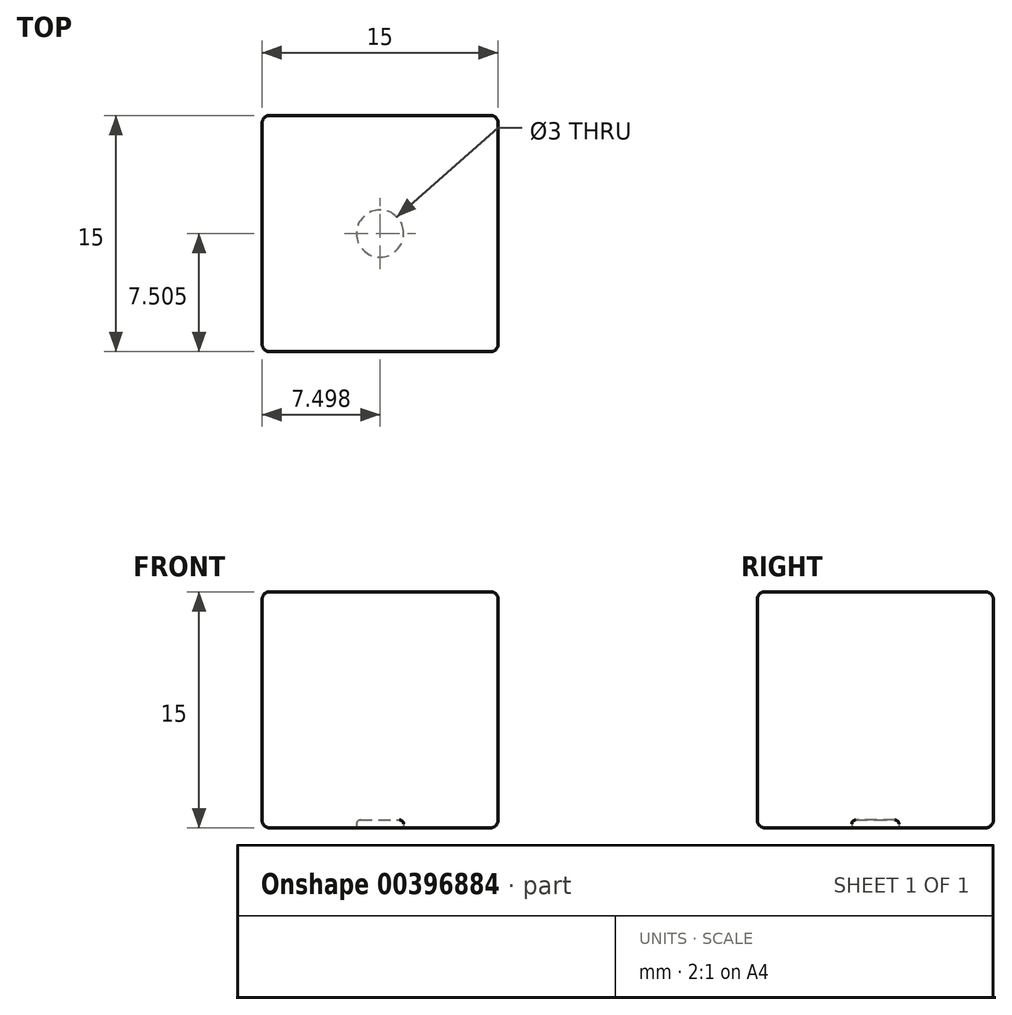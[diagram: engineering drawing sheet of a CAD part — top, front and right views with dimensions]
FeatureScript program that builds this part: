
annotation { "Feature Type Name" : "Feature", "Feature Type Description" : "" }
export const myFeature = defineFeature(function(context is Context, id is Id, definition is map)
    precondition{}
    {
        {
            var Q0;
            Q0=qCreatedBy(makeId("Top.planeOp"),FACE);
            var sketch = newSketch(context, id + "F0", { "sketchPlane" : qUnion([Q0])});
            skLineSegment(sketch, "E0.bottom", {"start": v(-9.53, -9.56) * mm, "end": v(5.47, -9.56) * mm});
            skLineSegment(sketch, "E0.top", {"start": v(-9.53, 5.44) * mm, "end": v(5.47, 5.44) * mm});
            skLineSegment(sketch, "E0.left", {"start": v(-9.53, -9.56) * mm, "end": v(-9.53, 5.44) * mm});
            skLineSegment(sketch, "E0.right", {"start": v(5.47, -9.56) * mm, "end": v(5.47, 5.44) * mm});
            skSolve(sketch);
        }
        {
            var Q0;
            Q0=makeQuery(id+"F0.imprint","IMPRINT",FACE,{"disambiguationData":[TD([[makeQuery(id+"F0.imprint","IMPRINT",EDGE,{"derivedFrom":sQuery(id+"F0.wireOp",EDGE,"E0.bottom")}),1.0]])]});
            var Q1;
            Q1=makeQuery(id+"F0.imprint","IMPRINT",FACE,{"disambiguationData":[TD([[makeQuery(id+"F0.imprint","IMPRINT",EDGE,{"derivedFrom":sQuery(id+"F0.wireOp",EDGE,"6saIbGSl-1DAX-xkG8-rUnz-SKyQh94YWWxh")}),1.0]])]});
            extrude(context, id + "F1", {"entities" : qUnion([Q0, Q1]), "depth" : 15 * mm});
        }
        {
            var Q0;
            Q0=makeQuery(id+"F1.opExtrude","CAP_FACE",FACE,{"disambiguationData":[OSD([sQuery(id+"F0.wireOp",EDGE,"E0.bottom"),sQuery(id+"F0.wireOp",EDGE,"E0.top"),sQuery(id+"F0.wireOp",EDGE,"E0.left"),sQuery(id+"F0.wireOp",EDGE,"E0.right")])],"isStart":true});
            var sketch = newSketch(context, id + "F2", { "sketchPlane" : qUnion([Q0])});
            skCircle(sketch, "E1", {"center": v(-2.03, 2.06) * mm, "radius": 1.5 * mm});
            skSolve(sketch);
        }
        {
            var Q0;
            Q0 = qSketchRegion(id + "F2", true);
            extrude(context, id + "F3", {"entities" : qUnion([Q0]), "operationType" : NewBodyOperationType.REMOVE, "oppositeDirection" : true, "depth" : 0.5 * mm});
        }
        {
            var Q0;
            Q0=makeQuery(id+"F1.opExtrude","SWEPT_EDGE",EDGE,{"disambiguationData":[OSD([sQuery(id+"F0.wireOp",EDGE,"E0.top"),sQuery(id+"F0.wireOp",EDGE,"E0.right")])]});
            var Q1;
            Q1=makeQuery(id+"F1.opExtrude","CAP_EDGE",EDGE,{"disambiguationData":[OSD([sQuery(id+"F0.wireOp",EDGE,"E0.top")])],"isStart":true});
            var Q2;
            Q2=makeQuery(id+"F1.opExtrude","CAP_EDGE",EDGE,{"disambiguationData":[OSD([sQuery(id+"F0.wireOp",EDGE,"E0.top")])],"isStart":false});
            var Q3;
            Q3=makeQuery(id+"F1.opExtrude","SWEPT_EDGE",EDGE,{"disambiguationData":[OSD([sQuery(id+"F0.wireOp",EDGE,"E0.top"),sQuery(id+"F0.wireOp",EDGE,"E0.left")])]});
            var Q4;
            Q4=makeQuery(id+"F1.opExtrude","CAP_EDGE",EDGE,{"disambiguationData":[OSD([sQuery(id+"F0.wireOp",EDGE,"E0.right")])],"isStart":true});
            var Q5;
            Q5=makeQuery(id+"F1.opExtrude","CAP_EDGE",EDGE,{"disambiguationData":[OSD([sQuery(id+"F0.wireOp",EDGE,"E0.right")])],"isStart":false});
            var Q6;
            Q6=makeQuery(id+"F1.opExtrude","SWEPT_EDGE",EDGE,{"disambiguationData":[OSD([sQuery(id+"F0.wireOp",EDGE,"E0.bottom"),sQuery(id+"F0.wireOp",EDGE,"E0.right")])]});
            var Q7;
            Q7=makeQuery(id+"F1.opExtrude","CAP_EDGE",EDGE,{"disambiguationData":[OSD([sQuery(id+"F0.wireOp",EDGE,"E0.left")])],"isStart":true});
            var Q8;
            Q8=makeQuery(id+"F1.opExtrude","CAP_EDGE",EDGE,{"disambiguationData":[OSD([sQuery(id+"F0.wireOp",EDGE,"E0.bottom")])],"isStart":true});
            var Q9;
            Q9=makeQuery(id+"F1.opExtrude","CAP_EDGE",EDGE,{"disambiguationData":[OSD([sQuery(id+"F0.wireOp",EDGE,"E0.left")])],"isStart":false});
            var Q10;
            Q10=makeQuery(id+"F1.opExtrude","SWEPT_EDGE",EDGE,{"disambiguationData":[OSD([sQuery(id+"F0.wireOp",EDGE,"E0.bottom"),sQuery(id+"F0.wireOp",EDGE,"E0.left")])]});
            var Q11;
            Q11=makeQuery(id+"F1.opExtrude","CAP_EDGE",EDGE,{"disambiguationData":[OSD([sQuery(id+"F0.wireOp",EDGE,"E0.bottom")])],"isStart":false});
            fillet(context, id + "F4", {"entities" : qUnion([Q0, Q1, Q2, Q3, Q4, Q5, Q6, Q7, Q8, Q9, Q10, Q11]), "radius" : 0.5 * mm, "tangentPropagation" : true, "allowEdgeOverflow" : false});
        }
        {
            var Q0;
            Q0=makeQuery(id+"F3.boolean.opBoolean","COPY",FACE,{"derivedFrom":makeQuery(id+"F3.opExtrude","CAP_FACE",FACE,{"disambiguationData":[OSD([sQuery(id+"F2.wireOp",EDGE,"E1")])],"isStart":false})});
            var Q1;
            Q1=makeQuery(id+"F3.boolean.opBoolean","COPY",EDGE,{"derivedFrom":makeQuery(id+"F3.opExtrude","CAP_EDGE",EDGE,{"disambiguationData":[OSD([sQuery(id+"F2.wireOp",EDGE,"E1")])],"isStart":true})});
            fillet(context, id + "F5", {"entities" : qUnion([Q0, Q1]), "radius" : 0.25 * mm, "tangentPropagation" : true, "allowEdgeOverflow" : false});
        }
    });
